# Revit family: Deca_Ducha Higiênica Unic_1984.C90.ACT.CR_Registro
name_source: partatom
category: Plumbing Fixtures
revit_build: Autodesk Revit Architecture 2012 (Build: 20110916_2132(x64)
units: mm (PartAtom-declared; Revit-internal decimal feet)

## types (2) — shared parameters
Aprovado por = Contino/quattroD
Assembly Code = D2010710
Atendimento ao Cliente = 0800-0117073
Consumo = Varia com a pressão
Criado por = Contino/quattroD
Default Elevation = 1200 mm
Description = Ducha higiênica com registro
Diâmetro Ponto de Agua = 15 mm  [stored 0.0492126 ft]
Flow Pressure = 0.00 psi
Informações Complementares = Mecanismo: 1/4 de volta
Linha = Unic
Louça/Metais = Metal
Manufacturer = Deca
Material = Deca_Latão Cromado e Plástico de Engenharia
Norma = ABNT NBR 14877 : 2002
Peso Liquido (Kg) = 1.01
Pressão = 2 A 40 mca
Produto = Ducha higiênica com registro
Raio Ponto de Agua = 8 mm  [stored 0.0262467 ft]
Segmento = Luxo
URL = www.deca.com.br/produtos
Variações de COR = Cromado (1984.C90.ACT.CR); Gold (1984.D90.ACT.GLD)
zero-valued in all types: CWFU, HWFU, WFU

## per-type parameters (varying)
| type | Código | Ducha Higiênica | Model |
| 1984.C90.ACT.CR_Cromado CR10 | 1984.C90.ACT.CR | Deca CR10 Cromado Metal | 1984.C90.ACT.CR |
| 1984.D90.ACT.GLD_Gold GLD | 1984.D90.ACT.GLD | Deca GLD Gold Metal | 1984.D90.ACT.GLD |

note: [stored X ft] marks values corroborated as IEEE doubles in the binary element streams (Revit-internal decimal feet)

## geometry (parser evidence)
native form markers: Blend x2, Sweep x2
no freeform markers — native parametric forms only
